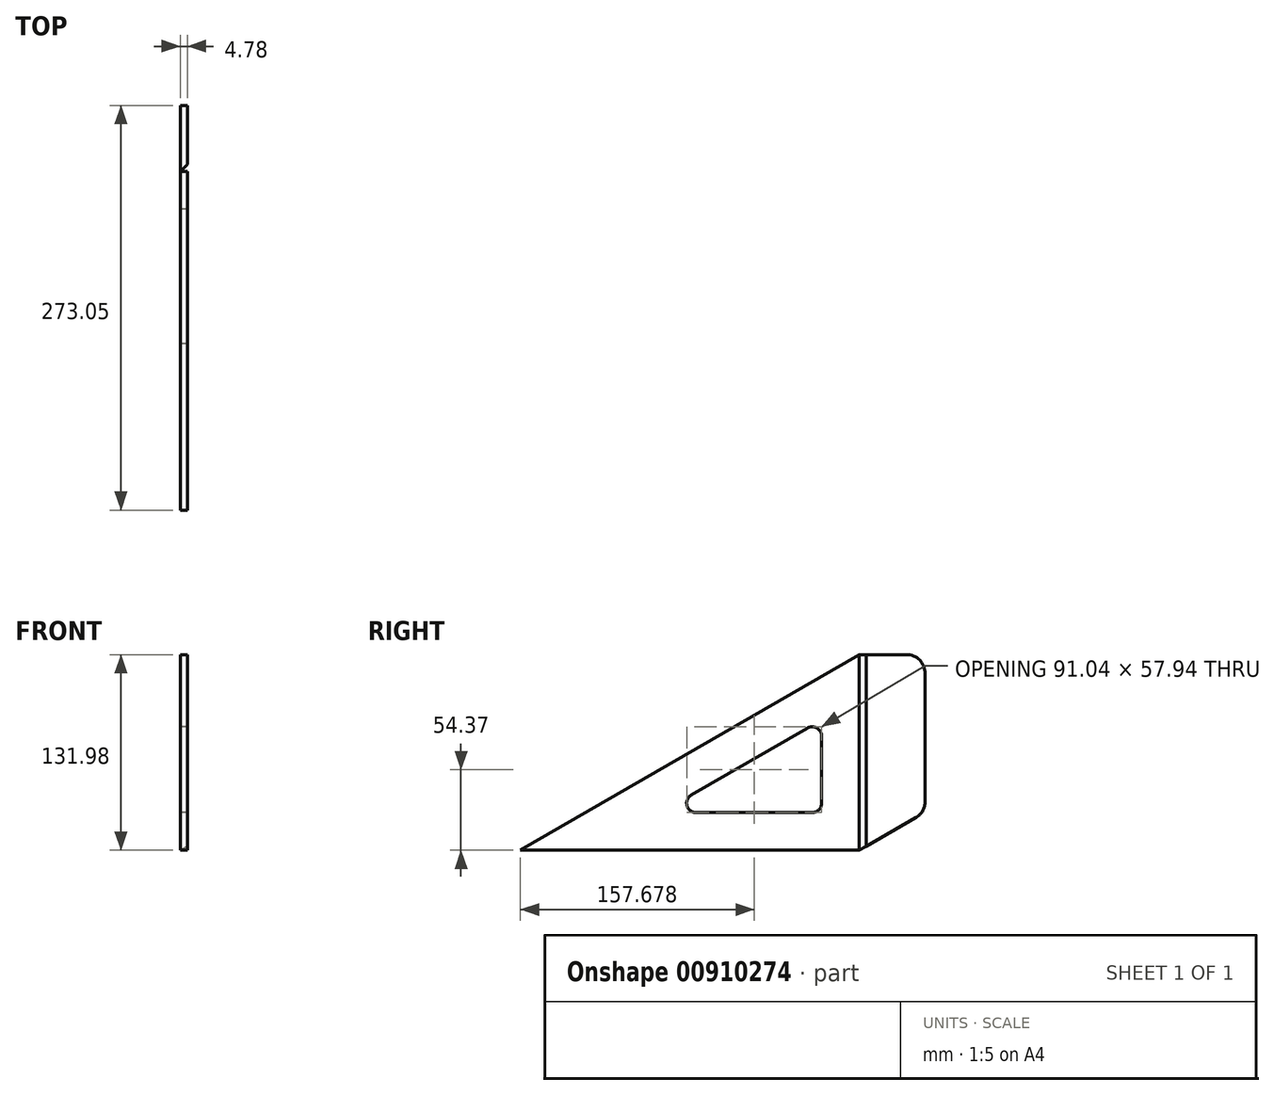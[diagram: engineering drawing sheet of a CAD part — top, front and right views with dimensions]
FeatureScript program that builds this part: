
annotation { "Feature Type Name" : "Feature", "Feature Type Description" : "" }
export const myFeature = defineFeature(function(context is Context, id is Id, definition is map)
    precondition{}
    {
        {
            var Q0;
            Q0=qCreatedBy(makeId("Right.planeOp"),FACE);
            var sketch = newSketch(context, id + "F0", { "sketchPlane" : qUnion([Q0])});
            skLineSegment(sketch, "E0", {"start": v(-228.6, 0) * mm, "end": v(0, 0) * mm});
            skLineSegment(sketch, "E1", {"start": v(0, 0) * mm, "end": v(0, 131.98) * mm});
            skLineSegment(sketch, "E2", {"start": v(0, 131.98) * mm, "end": v(-228.6, 0) * mm});
            skLineSegment(sketch, "E3.0", {"start": v(-25.4, 31.75) * mm, "end": v(-25.4, 76.99) * mm});
            skLineSegment(sketch, "E3.1", {"start": v(-110.1, 25.4) * mm, "end": v(-31.75, 25.4) * mm});
            skLineSegment(sketch, "E3.2", {"start": v(-34.93, 82.49) * mm, "end": v(-113.28, 37.25) * mm});
            skPoint(sketch, "E4.visualSharp", {"position": v(-133.8, 25.4) * mm});
            skArc(sketch, "E4.filletArc", {"start": v(-113.28, 37.25) * mm, "mid": v(-116.24, 30.1) * mm, "end": v(-110.1, 25.4) * mm});
            skPoint(sketch, "E5.visualSharp", {"position": v(-25.4, 87.99) * mm});
            skArc(sketch, "E5.filletArc", {"start": v(-25.4, 76.99) * mm, "mid": v(-28.58, 82.49) * mm, "end": v(-34.93, 82.49) * mm});
            skPoint(sketch, "E6.visualSharp", {"position": v(-25.4, 25.4) * mm});
            skArc(sketch, "E6.filletArc", {"start": v(-31.75, 25.4) * mm, "mid": v(-27.26, 27.26) * mm, "end": v(-25.4, 31.75) * mm});
            skPoint(sketch, "E7", {"position": v(0, 131.98) * mm});
            skSolve(sketch);
        }
        {
            var Q0;
            Q0 = qSketchRegion(id + "F0", true);
            extrude(context, id + "F1", {"entities" : qUnion([Q0]), "endBound" : BoundingType.SYMMETRIC, "depth" : 4.78 * mm, "offsetDistance" : 25.4 * mm});
        }
        {
            var Q0;
            Q0=qCreatedBy(makeId("Right.planeOp"),FACE);
            var sketch = newSketch(context, id + "F2", { "sketchPlane" : qUnion([Q0])});
            skLineSegment(sketch, "E8", {"start": v(0, 131.98) * mm, "end": v(31.75, 131.98) * mm});
            skLineSegment(sketch, "E9", {"start": v(44.45, 119.28) * mm, "end": v(44.45, 33) * mm});
            skLineSegment(sketch, "E10", {"start": v(38.1, 22) * mm, "end": v(0, 0) * mm});
            skLineSegment(sketch, "E11", {"start": v(0, 0) * mm, "end": v(0, 131.98) * mm});
            skPoint(sketch, "E12.visualSharp", {"position": v(44.45, 131.98) * mm});
            skArc(sketch, "E12.filletArc", {"start": v(44.45, 119.28) * mm, "mid": v(40.73, 128.26) * mm, "end": v(31.75, 131.98) * mm});
            skPoint(sketch, "E13.visualSharp", {"position": v(44.45, 25.66) * mm});
            skArc(sketch, "E13.filletArc", {"start": v(38.1, 22) * mm, "mid": v(42.75, 26.65) * mm, "end": v(44.45, 33) * mm});
            skLineSegment(sketch, "E14", {"start": v(0, 131.98) * mm, "end": v(0, 0) * mm});
            skSolve(sketch);
        }
        {
            var Q0;
            Q0 = qSketchRegion(id + "F2", true);
            extrude(context, id + "F3", {"entities" : qUnion([Q0]), "operationType" : NewBodyOperationType.ADD, "endBound" : BoundingType.SYMMETRIC, "depth" : 4.78 * mm, "offsetDistance" : 25.4 * mm});
        }
        {
            var Q0;
            Q0=qCreatedBy(makeId("Top.planeOp"),FACE);
            var sketch = newSketch(context, id + "F4", { "sketchPlane" : qUnion([Q0])});
            skLineSegment(sketch, "E15", {"start": v(-2.39, 0) * mm, "end": v(2.39, 0) * mm});
            skLineSegment(sketch, "E16", {"start": v(2.39, 0) * mm, "end": v(2.39, 4.78) * mm});
            skLineSegment(sketch, "E17", {"start": v(2.39, 4.78) * mm, "end": v(-2.39, 0) * mm});
            skSolve(sketch);
        }
        {
            var Q0;
            Q0 = qSketchRegion(id + "F4", true);
            extrude(context, id + "F5", {"entities" : qUnion([Q0]), "operationType" : NewBodyOperationType.REMOVE, "endBound" : BoundingType.THROUGH_ALL, "depth" : 25.4 * mm, "offsetDistance" : 25.4 * mm});
        }
    });
